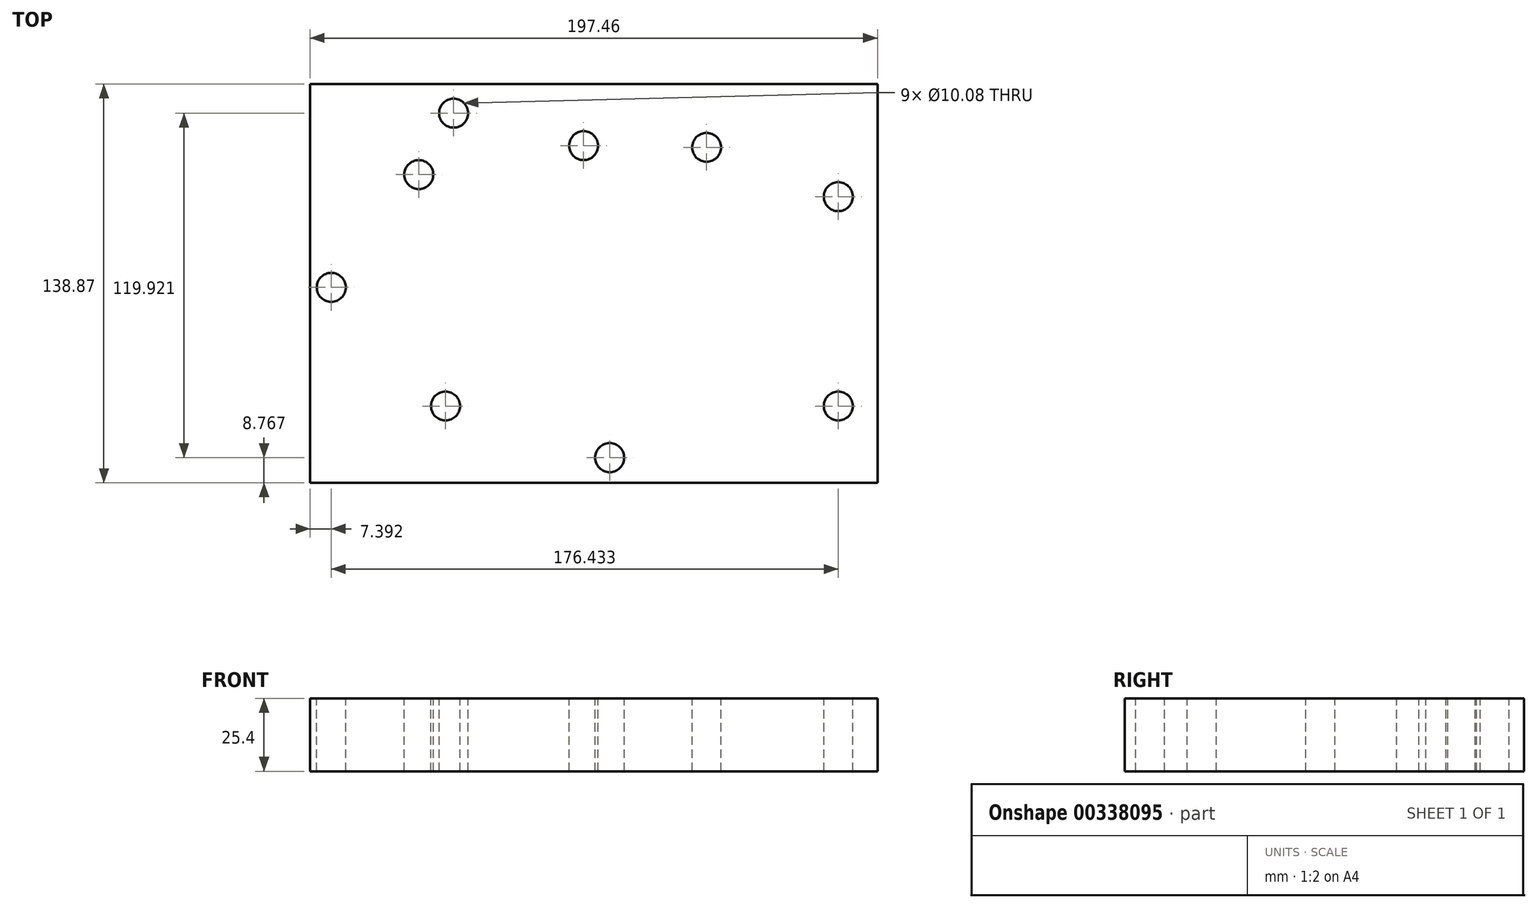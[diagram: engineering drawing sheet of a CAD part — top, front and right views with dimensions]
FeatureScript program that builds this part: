
annotation { "Feature Type Name" : "Feature", "Feature Type Description" : "" }
export const myFeature = defineFeature(function(context is Context, id is Id, definition is map)
    precondition{}
    {
        {
            var Q0;
            Q0=qCreatedBy(makeId("Top.planeOp"),FACE);
            var sketch = newSketch(context, id + "F0", { "sketchPlane" : qUnion([Q0])});
            skLineSegment(sketch, "E0.bottom", {"start": v(-117, 70.84) * mm, "end": v(80.47, 70.84) * mm});
            skLineSegment(sketch, "E0.top", {"start": v(-117, -68.03) * mm, "end": v(80.47, -68.03) * mm});
            skLineSegment(sketch, "E0.left", {"start": v(-117, 70.84) * mm, "end": v(-117, -68.03) * mm});
            skLineSegment(sketch, "E0.right", {"start": v(80.47, 70.84) * mm, "end": v(80.47, -68.03) * mm});
            skSolve(sketch);
        }
        {
            var Q0;
            Q0 = qSketchRegion(id + "F0", true);
            extrude(context, id + "F1", {"entities" : qUnion([Q0]), "depth" : 25.4 * mm});
        }
        {
            var Q0;
            Q0=makeQuery(id+"F1.opExtrude","CAP_FACE",FACE,{"disambiguationData":[OSD([sQuery(id+"F0.wireOp",EDGE,"E0.bottom"),sQuery(id+"F0.wireOp",EDGE,"E0.top"),sQuery(id+"F0.wireOp",EDGE,"E0.left"),sQuery(id+"F0.wireOp",EDGE,"E0.right")])],"isStart":false});
            var sketch = newSketch(context, id + "F2", { "sketchPlane" : qUnion([Q0])});
            skLineSegment(sketch, "E1.bottom", {"start": v(-69.84, 31.59) * mm, "end": v(66.83, 31.59) * mm, "construction": true});
            skLineSegment(sketch, "E1.top", {"start": v(-69.84, -41.3) * mm, "end": v(66.83, -41.3) * mm, "construction": true});
            skLineSegment(sketch, "E1.left", {"start": v(-69.84, 31.59) * mm, "end": v(-69.84, -41.3) * mm, "construction": true});
            skLineSegment(sketch, "E1.right", {"start": v(66.83, 31.59) * mm, "end": v(66.83, -41.3) * mm, "construction": true});
            skLineSegment(sketch, "E2.bottom", {"start": v(-109.6, 39.26) * mm, "end": v(-79.13, 39.26) * mm});
            skLineSegment(sketch, "E2.top", {"start": v(-109.6, 0) * mm, "end": v(-79.13, 0) * mm});
            skLineSegment(sketch, "E2.left", {"start": v(-109.6, 39.26) * mm, "end": v(-109.6, 0) * mm});
            skLineSegment(sketch, "E2.right", {"start": v(-79.13, 39.26) * mm, "end": v(-79.13, 0) * mm});
            skPoint(sketch, "E3", {"position": v(-21.8, 49.35) * mm});
            skPoint(sketch, "E4", {"position": v(21, 48.75) * mm});
            skPoint(sketch, "E5", {"position": v(-12.7, -59.26) * mm});
            skPoint(sketch, "E6", {"position": v(-67.02, 60.66) * mm});
            skSolve(sketch);
        }
        {
            var Q0;
            Q0=sQuery(id+"F2.wireOp",VERTEX,"E1.left.end");
            var Q1;
            Q1=sQuery(id+"F2.wireOp",VERTEX,"E2.right.start");
            var Q2;
            Q2=sQuery(id+"F2.wireOp",VERTEX,"E2.left.end");
            var Q3;
            Q3=sQuery(id+"F2.wireOp",VERTEX,"E1.top.end");
            var Q4;
            Q4=sQuery(id+"F2.wireOp",VERTEX,"E1.right.start");
            var Q5;
            Q5=sQuery(id+"F2.wireOp",VERTEX,"E3");
            var Q6;
            Q6=sQuery(id+"F2.wireOp",VERTEX,"E4");
            var Q7;
            Q7=sQuery(id+"F2.wireOp",VERTEX,"E6");
            var Q8;
            Q8=sQuery(id+"F2.wireOp",VERTEX,"E5");
            var Q9;
            Q9=makeQuery(id+"F1.opExtrude","SWEPT_BODY",BODY,{"disambiguationData":[OSD([sQuery(id+"F0.wireOp",EDGE,"E0.bottom"),sQuery(id+"F0.wireOp",EDGE,"E0.top"),sQuery(id+"F0.wireOp",EDGE,"E0.left"),sQuery(id+"F0.wireOp",EDGE,"E0.right")])]});
            hole(context, id + "F3", {"style" : HoleStyle.SIMPLE, "endStyle" : HoleEndStyle.THROUGH, "standardTappedOrClearance" : lookupTablePath({ "standard" : "ANSI", "fit" : "Normal (ASME)", "size" : "3/8", "type" : "Clearance" }), "standardBlindInLast" : lookupTablePath({ "fit" : "Free", "standard" : "ANSI", "size" : "3/8", "type" : "Clearance" }), "holeDiameter" : 10.08 * mm, "tappedDepth" : 12.7 * mm, "tapClearance" : 3, "locations" : qUnion([Q0, Q1, Q2, Q3, Q4, Q5, Q6, Q7, Q8]), "scope" : qUnion([Q9])});
        }
    });
